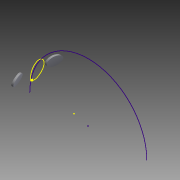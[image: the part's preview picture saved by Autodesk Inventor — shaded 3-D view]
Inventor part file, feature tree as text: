
AUTODESK INVENTOR PART (.ipt)
format: ipt  version: 2015 (Build 190159000, 159)  size: 117,760 bytes
history: native  units: in
note: dims shown in document units (in); Inventor stores cm internally (conversion verified against a paired STEP export)
features: reference x4, sketch x3, extrude x1, revolve x1
ambient origin geometry x8: Origin, YZ Plane, XZ Plane, XY Plane, X Axis, Y Axis, Z Axis, Center Point
bodies: Solid1 (feature_tree)
feature tree (9):
  sketch  "Sketch1"  dims[d0=0.1in d1=0.1in]
  extrude  "Extrusion1"  Depth=0.1in
  revolve  "Revolution1"  [1 undecoded]
  reference  "Reference1"
  sketch  "Sketch2"  dims[d2=0.025in d3=0.025in]
  reference  "Reference2"
  reference  "Reference3"
  sketch  "Sketch3"  dims[d4=0.035in d5=0.035in d6=1.0in d7=0.0in d8=0.035in d9=90.0deg d10=0.02in]
  reference  "Reference4"
note: 1 required parameter value undecoded (feature->parameter linkage not recoverable at this tier; creation-order binding heuristic only, values carry confidence <= 0.55)
